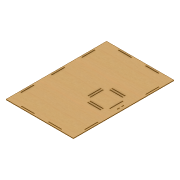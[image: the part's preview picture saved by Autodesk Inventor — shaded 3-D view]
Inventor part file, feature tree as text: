
AUTODESK INVENTOR PART (.ipt)
format: ipt  version: 2021 (Build 250183000, 183)  size: 230,912 bytes
history: native  units: mm
features: sketch x2, other x1, extrude x1, hole x1
ambient origin geometry x8: Origin, YZ Plane, XZ Plane, XY Plane, X Axis, Y Axis, Z Axis, Center Point
bodies: Body1 (feature_tree)
feature tree (5):
  other  "Твердое тело1"
  extrude  "Выдавливание1"  Depth=140.0mm
  hole  "Отверстие1"  [1 undecoded]
  sketch  "Эскиз1"
  sketch  "Эскиз3"
note: 1 required parameter value undecoded (feature->parameter linkage not recoverable at this tier; creation-order binding heuristic only, values carry confidence <= 0.55)
